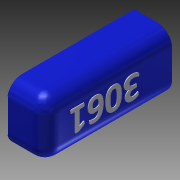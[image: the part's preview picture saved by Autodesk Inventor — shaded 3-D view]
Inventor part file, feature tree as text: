
AUTODESK INVENTOR PART (.ipt)
format: ipt  version: 2014 SP1 (Build 180222100, 222)  size: 362,496 bytes
history: native  units: in
note: dims shown in document units (in); Inventor stores cm internally (conversion verified against a paired STEP export)
features: extrude x4, reference x4, sketch x3, fillet x1, projected_geometry x1
ambient origin geometry x8: Origin, YZ Plane, XZ Plane, XY Plane, X Axis, Y Axis, Z Axis, Center Point
bodies: Solid1 (feature_tree)
feature tree (13):
  sketch  "Sketch1"  dims[d0=0.0625in d1=0.0in d3=1.0in]
  extrude  "Extrusion1"  Depth=1.0in
  extrude  "Extrusion2"  Depth=0.0625in
  extrude  "Extrusion3"  Depth=0.0625in TaperAngle=0.0deg
  fillet  "Fillet1"  Radius=1.3125in
  extrude  "Extrusion4"  Depth=6.0in
  reference  "Reference4"
  reference  "Reference5"
  sketch  "Sketch2"  dims[d7=1.0in d9=0.0625in]
  sketch  "Sketch3"  dims[d10=11.25in d11=0.0in d12=0.0625in d13=0.0in d14=1.3125in d15=6.0in d17=1.0in d18=0.0625in d19=0.0in d20=0.0625in d21=0.0625in]
  reference  "Reference6"
  projected_geometry  "Projected Loop1"
  reference  "Reference7"
